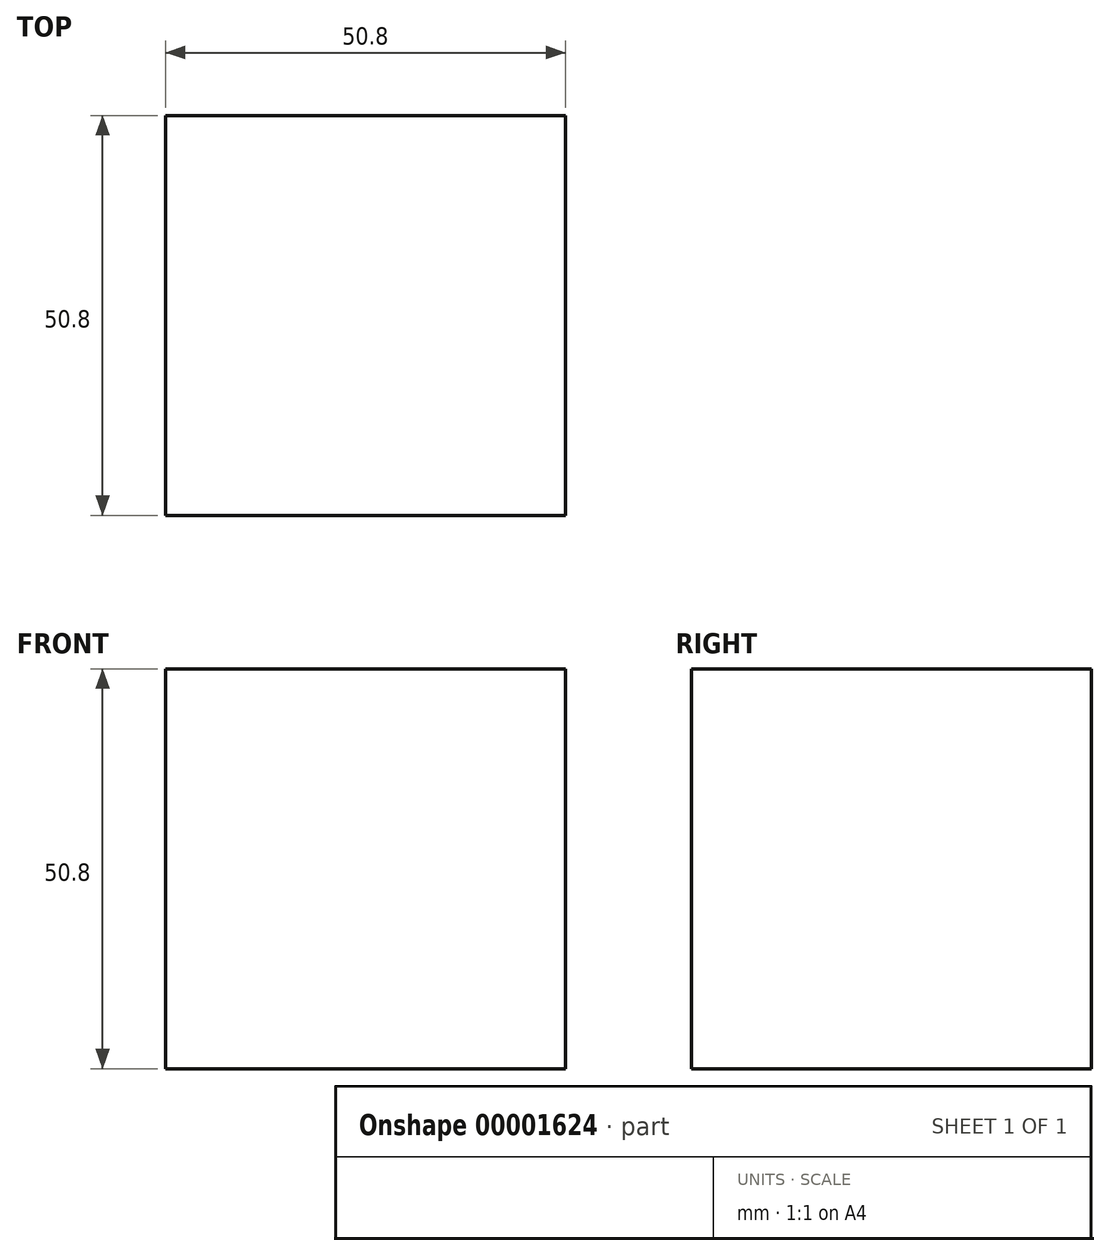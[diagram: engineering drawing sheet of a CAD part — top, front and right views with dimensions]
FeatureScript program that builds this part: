
annotation { "Feature Type Name" : "Feature", "Feature Type Description" : "" }
export const myFeature = defineFeature(function(context is Context, id is Id, definition is map)
    precondition{}
    {
        {
            var Q0;
            Q0=qCreatedBy(makeId("Top.planeOp"),FACE);
            var sketch = newSketch(context, id + "F0", { "sketchPlane" : qUnion([Q0])});
            skLineSegment(sketch, "E0.bottom", {"start": v(0, 0) * mm, "end": v(50.8, 0) * mm});
            skLineSegment(sketch, "E0.top", {"start": v(0, 50.8) * mm, "end": v(50.8, 50.8) * mm});
            skLineSegment(sketch, "E0.left", {"start": v(0, 0) * mm, "end": v(0, 50.8) * mm});
            skLineSegment(sketch, "E0.right", {"start": v(50.8, 0) * mm, "end": v(50.8, 50.8) * mm});
            skSolve(sketch);
        }
        {
            var Q0;
            Q0 = qSketchRegion(id + "F0", true);
            extrude(context, id + "F1", {"entities" : qUnion([Q0]), "depth" : 25.4 * mm});
        }
        {
            var Q0;
            Q0=makeQuery(id+"F1.opExtrude","CAP_FACE",FACE,{"disambiguationData":[OSD([sQuery(id+"F0.wireOp",EDGE,"E0.bottom"),sQuery(id+"F0.wireOp",EDGE,"E0.top"),sQuery(id+"F0.wireOp",EDGE,"E0.left"),sQuery(id+"F0.wireOp",EDGE,"E0.right")])],"isStart":false});
            extrude(context, id + "F2", {"entities" : qUnion([Q0]), "operationType" : NewBodyOperationType.ADD, "depth" : 25.4 * mm});
        }
    });
